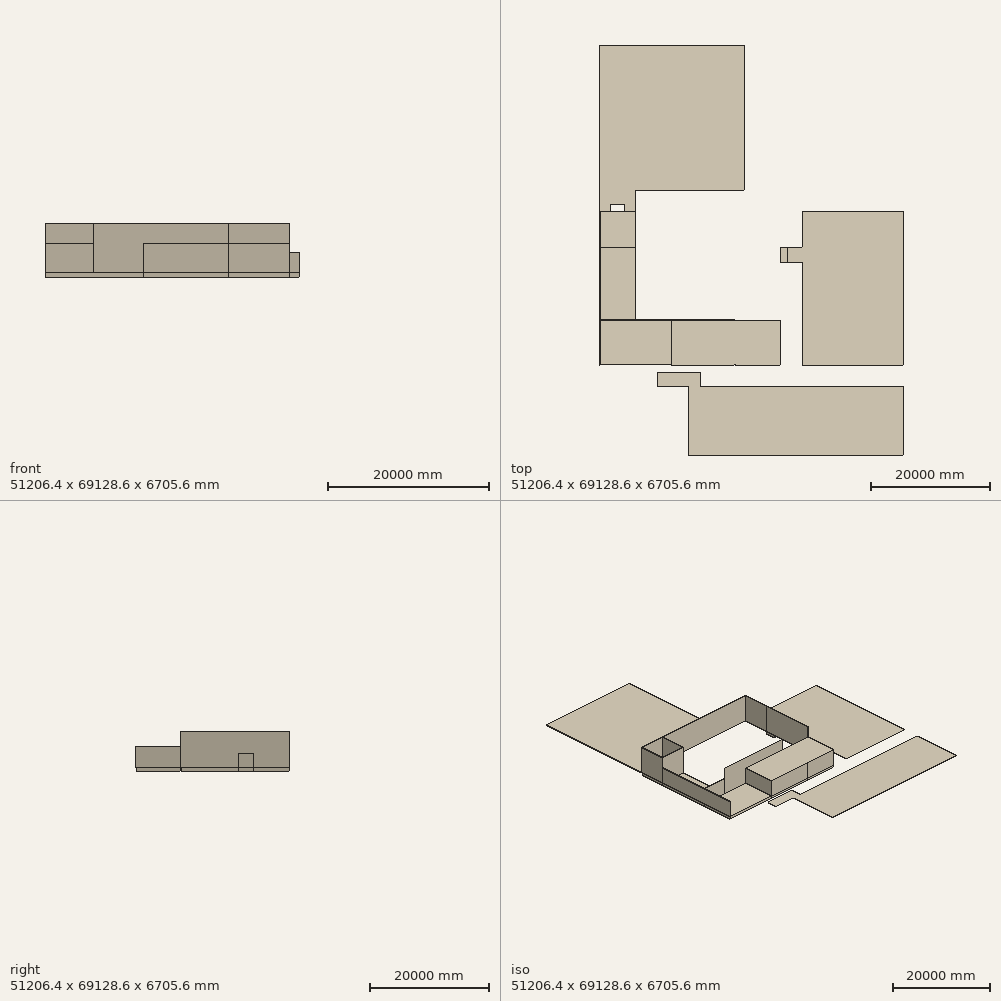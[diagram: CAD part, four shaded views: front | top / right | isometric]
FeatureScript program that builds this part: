
annotation { "Feature Type Name" : "Feature", "Feature Type Description" : "" }
export const myFeature = defineFeature(function(context is Context, id is Id, definition is map)
    precondition{}
    {
        {
            var Q0;
            Q0=qCreatedBy(makeId("Top.planeOp"),FACE);
            var sketch = newSketch(context, id + "F0", { "sketchPlane" : qUnion([Q0])});
            skLineSegment(sketch, "E0.bottom", {"start": v(-25389.28, -17373.6) * mm, "end": v(-36057.28, -17373.6) * mm});
            skLineSegment(sketch, "E0.left", {"start": v(-25389.28, -17373.6) * mm, "end": v(-25389.28, -9753.6) * mm});
            skLineSegment(sketch, "E0.right", {"start": v(-36057.28, -17373.6) * mm, "end": v(-36057.28, -9753.6) * mm});
            skLineSegment(sketch, "E1.bottom", {"start": v(-36057.28, -17373.6) * mm, "end": v(-48249.28, -17373.6) * mm});
            skLineSegment(sketch, "E1.top", {"start": v(-37581.28, -9753.6) * mm, "end": v(-48249.28, -9753.6) * mm});
            skLineSegment(sketch, "E1.right", {"start": v(-48249.28, -17373.6) * mm, "end": v(-48249.28, -9753.6) * mm});
            skLineSegment(sketch, "E2.top", {"start": v(-25389.28, -17373.6) * mm, "end": v(-17769.28, -17373.6) * mm});
            skLineSegment(sketch, "E2.left", {"start": v(-25389.28, -9753.6) * mm, "end": v(-25389.28, -17373.6) * mm});
            skLineSegment(sketch, "E3.bottom", {"start": v(-48249.28, -9753.6) * mm, "end": v(-42153.28, -9753.6) * mm});
            skLineSegment(sketch, "E3.top", {"start": v(-48249.28, 2438.4) * mm, "end": v(-42153.28, 2438.4) * mm});
            skLineSegment(sketch, "E3.left", {"start": v(-48249.28, -9753.6) * mm, "end": v(-48249.28, 2438.4) * mm});
            skLineSegment(sketch, "E3.right", {"start": v(-42153.28, -9753.6) * mm, "end": v(-42153.28, 2438.4) * mm});
            skLineSegment(sketch, "E4.bottom", {"start": v(-42153.28, -9753.6) * mm, "end": v(-17769.28, -9753.6) * mm});
            skLineSegment(sketch, "E4.top", {"start": v(-17830.23, 2438.4) * mm, "end": v(-17769.28, 2438.4) * mm});
            skLineSegment(sketch, "E4.right", {"start": v(-17769.28, -9753.6) * mm, "end": v(-17769.28, 2438.4) * mm});
            skLineSegment(sketch, "E5.top", {"start": v(-48249.28, 8534.4) * mm, "end": v(-42153.28, 8534.4) * mm});
            skLineSegment(sketch, "E5.left", {"start": v(-48249.28, 2438.4) * mm, "end": v(-48249.28, 8534.4) * mm});
            skLineSegment(sketch, "E5.right", {"start": v(-42153.28, 2438.4) * mm, "end": v(-42153.28, 8534.4) * mm});
            skLineSegment(sketch, "E6.bottom", {"start": v(-42153.28, 8534.4) * mm, "end": v(-36057.28, 8534.4) * mm});
            skLineSegment(sketch, "E6.left", {"start": v(-42153.28, 8534.4) * mm, "end": v(-42153.28, 2438.4) * mm});
            skLineSegment(sketch, "E6.right", {"start": v(-36057.28, 8534.4) * mm, "end": v(-36057.28, 8473.44) * mm});
            skLineSegment(sketch, "E7.bottom", {"start": v(-36057.28, 8534.4) * mm, "end": v(-31485.28, 8534.4) * mm});
            skLineSegment(sketch, "E7.right", {"start": v(-31485.28, 8534.4) * mm, "end": v(-31485.28, 8473.44) * mm});
            skLineSegment(sketch, "E8.bottom", {"start": v(-31485.28, 8534.4) * mm, "end": v(-17769.28, 8534.4) * mm});
            skLineSegment(sketch, "E8.right", {"start": v(-17769.28, 8534.4) * mm, "end": v(-17769.28, 2438.4) * mm});
            skLineSegment(sketch, "E9.bottom", {"start": v(-46420.48, 8534.4) * mm, "end": v(-43982.08, 8534.4) * mm});
            skLineSegment(sketch, "E9.top", {"start": v(-46420.48, 9753.6) * mm, "end": v(-43982.08, 9753.6) * mm});
            skLineSegment(sketch, "E9.left", {"start": v(-46420.48, 9753.6) * mm, "end": v(-46420.48, 8534.4) * mm});
            skLineSegment(sketch, "E9.right", {"start": v(-43982.08, 9753.6) * mm, "end": v(-43982.08, 8534.4) * mm});
            skLineSegment(sketch, "E10.bottom", {"start": v(-38495.68, -17373.6) * mm, "end": v(-36057.28, -17373.6) * mm});
            skLineSegment(sketch, "E10.top", {"start": v(-38495.68, -18592.8) * mm, "end": v(-36057.28, -18592.8) * mm});
            skLineSegment(sketch, "E10.left", {"start": v(-38495.68, -17373.6) * mm, "end": v(-38495.68, -18592.8) * mm});
            skLineSegment(sketch, "E10.right", {"start": v(-36057.28, -17373.6) * mm, "end": v(-36057.28, -18592.8) * mm});
            skLineSegment(sketch, "E11.bottom", {"start": v(-17769.28, 2438.4) * mm, "end": v(-16550.08, 2438.4) * mm});
            skLineSegment(sketch, "E11.top", {"start": v(-17769.28, 0) * mm, "end": v(-16550.08, 0) * mm});
            skLineSegment(sketch, "E11.left", {"start": v(-17769.28, 2438.4) * mm, "end": v(-17769.28, 0) * mm});
            skLineSegment(sketch, "E11.right", {"start": v(-16550.08, 2438.4) * mm, "end": v(-16550.08, 0) * mm});
            skLineSegment(sketch, "E12.0", {"start": v(-48188.32, 8473.44) * mm, "end": v(-42214.24, 8473.44) * mm});
            skLineSegment(sketch, "E12.1", {"start": v(-48188.32, 2499.36) * mm, "end": v(-48188.32, 8473.44) * mm});
            skLineSegment(sketch, "E12.2", {"start": v(-48188.32, 2499.36) * mm, "end": v(-42214.24, 2499.36) * mm});
            skLineSegment(sketch, "E12.3", {"start": v(-42214.24, 2499.36) * mm, "end": v(-42214.24, 8473.44) * mm});
            skLineSegment(sketch, "E13.1", {"start": v(-31485.28, 8473.44) * mm, "end": v(-17830.24, 8473.44) * mm});
            skLineSegment(sketch, "E13.2", {"start": v(-36057.28, 8473.44) * mm, "end": v(-31485.28, 8473.44) * mm});
            skLineSegment(sketch, "E13.3", {"start": v(-42153.28, 8473.44) * mm, "end": v(-36057.28, 8473.44) * mm});
            skLineSegment(sketch, "E14.0", {"start": v(-17830.23, -9753.6) * mm, "end": v(-17830.23, 2438.4) * mm});
            skLineSegment(sketch, "E15", {"start": v(-17769.28, -17373.6) * mm, "end": v(-17769.28, -9753.6) * mm});
            skLineSegment(sketch, "E16.0", {"start": v(-25389.28, -17312.64) * mm, "end": v(-36057.28, -17312.64) * mm});
            skLineSegment(sketch, "E16.1", {"start": v(-25389.28, -17312.64) * mm, "end": v(-17830.24, -17312.64) * mm});
            skLineSegment(sketch, "E16.2", {"start": v(-17830.24, -17312.64) * mm, "end": v(-17830.24, -9753.6) * mm});
            skLineSegment(sketch, "E17.0", {"start": v(-42153.28, -9814.56) * mm, "end": v(-17769.28, -9814.56) * mm});
            skLineSegment(sketch, "E18.0", {"start": v(-25450.24, -9753.6) * mm, "end": v(-25450.24, -17373.6) * mm});
            skLineSegment(sketch, "E19.0", {"start": v(-35996.32, -17373.6) * mm, "end": v(-35996.32, -9753.6) * mm});
            skLineSegment(sketch, "E20.0", {"start": v(-36057.28, -17312.64) * mm, "end": v(-48249.28, -17312.64) * mm});
            skLineSegment(sketch, "E21.0", {"start": v(-48188.32, -17373.6) * mm, "end": v(-48188.32, -9753.6) * mm});
            skLineSegment(sketch, "E22.0", {"start": v(-48188.32, -9753.6) * mm, "end": v(-48188.32, 2438.4) * mm});
            skLineSegment(sketch, "E23.0", {"start": v(-48249.28, -9814.56) * mm, "end": v(-42153.28, -9814.56) * mm});
            skLineSegment(sketch, "E24.0", {"start": v(-42214.24, -9753.6) * mm, "end": v(-42214.24, 2438.4) * mm});
            skLineSegment(sketch, "E25", {"start": v(-17830.24, 8473.44) * mm, "end": v(-17769.28, 8534.4) * mm});
            skLineSegment(sketch, "E26", {"start": v(-17830.23, 2438.4) * mm, "end": v(-17830.24, 8473.44) * mm});
            skLineSegment(sketch, "E27", {"start": v(-42214.24, -9753.6) * mm, "end": v(-42214.24, -9814.56) * mm});
            skLineSegment(sketch, "E28.bottom", {"start": v(-14111.68, 8473.44) * mm, "end": v(2957.12, 8473.44) * mm});
            skLineSegment(sketch, "E28.top", {"start": v(-14111.68, -17434.56) * mm, "end": v(2957.12, -17434.56) * mm});
            skLineSegment(sketch, "E28.left", {"start": v(-14111.68, 8473.44) * mm, "end": v(-14111.68, -17434.56) * mm});
            skLineSegment(sketch, "E28.right", {"start": v(2957.12, 8473.44) * mm, "end": v(2957.12, -17434.56) * mm});
            skLineSegment(sketch, "E29.bottom", {"start": v(-33314.08, -32613.6) * mm, "end": v(2957.12, -32613.6) * mm});
            skLineSegment(sketch, "E29.top", {"start": v(-33314.08, -21031.2) * mm, "end": v(2957.12, -21031.2) * mm});
            skLineSegment(sketch, "E29.left", {"start": v(-33314.08, -32613.6) * mm, "end": v(-33314.08, -21031.2) * mm});
            skLineSegment(sketch, "E29.right", {"start": v(2957.12, -32613.6) * mm, "end": v(2957.12, -21031.2) * mm});
            skLineSegment(sketch, "E30.top", {"start": v(-14111.68, -21031.2) * mm, "end": v(2957.12, -21031.2) * mm});
            skLineSegment(sketch, "E30.left", {"start": v(-14111.68, -17434.56) * mm, "end": v(-14111.68, -21031.2) * mm});
            skLineSegment(sketch, "E30.right", {"start": v(2957.12, -17434.56) * mm, "end": v(2957.12, -21031.2) * mm});
            skLineSegment(sketch, "E31.bottom", {"start": v(-8625.28, 8473.44) * mm, "end": v(-2529.28, 8473.44) * mm});
            skLineSegment(sketch, "E31.top", {"start": v(-8625.28, 42001.44) * mm, "end": v(-2529.28, 42001.44) * mm});
            skLineSegment(sketch, "E31.left", {"start": v(-8625.28, 8473.44) * mm, "end": v(-8625.28, 42001.44) * mm});
            skLineSegment(sketch, "E31.right", {"start": v(-2529.28, 8473.44) * mm, "end": v(-2529.28, 42001.44) * mm});
            skLineSegment(sketch, "E32.bottom", {"start": v(-48249.28, 36515.04) * mm, "end": v(-23865.28, 36515.04) * mm});
            skLineSegment(sketch, "E32.top", {"start": v(-48249.28, 12131.04) * mm, "end": v(-23865.28, 12131.04) * mm});
            skLineSegment(sketch, "E32.left", {"start": v(-48249.28, 36515.04) * mm, "end": v(-48249.28, 12131.04) * mm});
            skLineSegment(sketch, "E32.right", {"start": v(-23865.28, 36515.04) * mm, "end": v(-23865.28, 12131.04) * mm});
            skLineSegment(sketch, "E33.bottom", {"start": v(-23865.28, 36515.04) * mm, "end": v(-34533.28, 36515.04) * mm});
            skLineSegment(sketch, "E33.top", {"start": v(-23865.28, 42611.04) * mm, "end": v(-34533.28, 42611.04) * mm});
            skLineSegment(sketch, "E33.left", {"start": v(-23865.28, 36515.04) * mm, "end": v(-23865.28, 42611.04) * mm});
            skLineSegment(sketch, "E33.right", {"start": v(-34533.28, 36515.04) * mm, "end": v(-34533.28, 42611.04) * mm});
            skLineSegment(sketch, "E34.bottom", {"start": v(-48249.28, 12131.04) * mm, "end": v(-42153.28, 12131.04) * mm});
            skLineSegment(sketch, "E34.left", {"start": v(-48249.28, 12131.04) * mm, "end": v(-48249.28, 8534.4) * mm});
            skLineSegment(sketch, "E34.right", {"start": v(-42153.28, 12131.04) * mm, "end": v(-42153.28, 8534.4) * mm});
            skLineSegment(sketch, "E35.bottom", {"start": v(-16550.08, 2438.4) * mm, "end": v(-14111.68, 2438.4) * mm});
            skLineSegment(sketch, "E35.top", {"start": v(-16550.08, 0) * mm, "end": v(-14111.68, 0) * mm});
            skLineSegment(sketch, "E35.right", {"start": v(-14111.68, 2438.4) * mm, "end": v(-14111.68, 0) * mm});
            skLineSegment(sketch, "E36.bottom", {"start": v(-38495.68, -18592.8) * mm, "end": v(-31248.17, -18592.8) * mm});
            skLineSegment(sketch, "E36.top", {"start": v(-38495.68, -21031.2) * mm, "end": v(-31248.17, -21031.2) * mm});
            skLineSegment(sketch, "E36.left", {"start": v(-38495.68, -18592.8) * mm, "end": v(-38495.68, -21031.2) * mm});
            skLineSegment(sketch, "E36.right", {"start": v(-31248.17, -18592.8) * mm, "end": v(-31248.17, -21031.2) * mm});
            skSolve(sketch);
        }
        {
            var Q0;
            {var subQ1=sQuery(id+"F0.wireOp",EDGE,"E2.left");var subQ3=sQuery(id+"F0.wireOp",EDGE,"E17.0");var subQ4=makeQuery(id+"F0.imprint","INTERSECT",VERTEX,{"derivedFrom":[subQ1,subQ3]});Q0=makeQuery(id+"F0.imprint","IMPRINT",FACE,{"disambiguationData":[TD([[makeQuery(id+"F0.imprint","IMPRINT",EDGE,{"disambiguationData":[TD([[subQ4,1.0]])],"derivedFrom":subQ3}),-1.0]])]});}
            var Q1;
            {var subQ0=sQuery(id+"F0.wireOp",EDGE,"E4.bottom");var subQ1=sQuery(id+"F0.wireOp",EDGE,"E2.left");var subQ2=makeQuery(id+"F0.imprint","INTERSECT",VERTEX,{"derivedFrom":[subQ1,subQ0]});Q1=makeQuery(id+"F0.imprint","IMPRINT",FACE,{"disambiguationData":[TD([[makeQuery(id+"F0.imprint","IMPRINT",EDGE,{"disambiguationData":[TD([[subQ2,-1.0]])],"derivedFrom":subQ1}),-1.0]])]});}
            var Q2;
            {var subQ0=sQuery(id+"F0.wireOp",EDGE,"E18.0");var subQ1=sQuery(id+"F0.wireOp",EDGE,"E4.bottom");var subQ2=makeQuery(id+"F0.imprint","INTERSECT",VERTEX,{"derivedFrom":[subQ1,subQ0]});Q2=makeQuery(id+"F0.imprint","IMPRINT",FACE,{"disambiguationData":[TD([[makeQuery(id+"F0.imprint","IMPRINT",EDGE,{"disambiguationData":[TD([[subQ2,1.0]])],"derivedFrom":subQ1}),-1.0]])]});}
            var Q3;
            {var subQ0=sQuery(id+"F0.wireOp",EDGE,"E4.bottom");var subQ13=makeQuery(id+"F0.imprint","IMPRINT",VERTEX,{"derivedFrom":subQ0});Q3=makeQuery(id+"F0.imprint","IMPRINT",FACE,{"disambiguationData":[TD([[makeQuery(id+"F0.imprint","IMPRINT",EDGE,{"disambiguationData":[TD([[subQ13,-1.0]])],"derivedFrom":subQ0}),-1.0]])]});}
            var Q4;
            {var subQ0=sQuery(id+"F0.wireOp",EDGE,"E3.bottom");var subQ5=sQuery(id+"F0.wireOp",EDGE,"E21.0");var subQ6=makeQuery(id+"F0.imprint","INTERSECT",VERTEX,{"derivedFrom":[subQ0,subQ5]});Q4=makeQuery(id+"F0.imprint","IMPRINT",FACE,{"disambiguationData":[TD([[makeQuery(id+"F0.imprint","IMPRINT",EDGE,{"disambiguationData":[TD([[subQ6,1.0]])],"derivedFrom":subQ5}),1.0]])]});}
            var Q5;
            {var subQ0=sQuery(id+"F0.wireOp",EDGE,"E3.left");Q5=makeQuery(id+"F0.imprint","IMPRINT",FACE,{"disambiguationData":[TD([[makeQuery(id+"F0.imprint","IMPRINT",EDGE,{"derivedFrom":subQ0}),-1.0]])]});}
            var Q6;
            {var subQ0=sQuery(id+"F0.wireOp",EDGE,"E20.0");var subQ1=sQuery(id+"F0.wireOp",EDGE,"E1.right");var subQ2=makeQuery(id+"F0.imprint","INTERSECT",VERTEX,{"derivedFrom":[subQ1,subQ0]});Q6=makeQuery(id+"F0.imprint","IMPRINT",FACE,{"disambiguationData":[TD([[makeQuery(id+"F0.imprint","IMPRINT",EDGE,{"disambiguationData":[TD([[subQ2,-1.0]])],"derivedFrom":subQ1}),-1.0]])]});}
            var Q7;
            {var subQ0=sQuery(id+"F0.wireOp",EDGE,"E10.bottom");Q7=makeQuery(id+"F0.imprint","IMPRINT",FACE,{"disambiguationData":[TD([[makeQuery(id+"F0.imprint","IMPRINT",EDGE,{"derivedFrom":subQ0}),1.0]])]});}
            var Q8;
            {var subQ0=sQuery(id+"F0.wireOp",EDGE,"E0.right");var subQ5=sQuery(id+"F0.wireOp",EDGE,"E16.0");var subQ7=makeQuery(id+"F0.imprint","INTERSECT",VERTEX,{"derivedFrom":[subQ0,subQ5]});Q8=makeQuery(id+"F0.imprint","IMPRINT",FACE,{"disambiguationData":[TD([[makeQuery(id+"F0.imprint","IMPRINT",EDGE,{"disambiguationData":[TD([[subQ7,1.0]])],"derivedFrom":subQ5}),1.0]])]});}
            var Q9;
            {var subQ0=sQuery(id+"F0.wireOp",EDGE,"E0.right");var subQ6=sQuery(id+"F0.wireOp",EDGE,"E16.0");var subQ7=makeQuery(id+"F0.imprint","INTERSECT",VERTEX,{"derivedFrom":[subQ0,subQ6]});Q9=makeQuery(id+"F0.imprint","IMPRINT",FACE,{"disambiguationData":[TD([[makeQuery(id+"F0.imprint","IMPRINT",EDGE,{"disambiguationData":[TD([[subQ7,-1.0]])],"derivedFrom":subQ0}),-1.0]])]});}
            var Q10;
            {var subQ0=sQuery(id+"F0.wireOp",EDGE,"E18.0");var subQ1=sQuery(id+"F0.wireOp",EDGE,"E0.bottom");var subQ2=makeQuery(id+"F0.imprint","INTERSECT",VERTEX,{"derivedFrom":[subQ1,subQ0]});Q10=makeQuery(id+"F0.imprint","IMPRINT",FACE,{"disambiguationData":[TD([[makeQuery(id+"F0.imprint","IMPRINT",EDGE,{"disambiguationData":[TD([[subQ2,-1.0]])],"derivedFrom":subQ1}),-1.0]])]});}
            var Q11;
            {var subQ2=sQuery(id+"F0.wireOp",EDGE,"E2.top");Q11=makeQuery(id+"F0.imprint","IMPRINT",FACE,{"disambiguationData":[TD([[makeQuery(id+"F0.imprint","IMPRINT",EDGE,{"derivedFrom":subQ2}),1.0]])]});}
            var Q12;
            {var subQ0=sQuery(id+"F0.wireOp",EDGE,"E4.bottom");var subQ1=sQuery(id+"F0.wireOp",EDGE,"E2.left");var subQ2=makeQuery(id+"F0.imprint","INTERSECT",VERTEX,{"derivedFrom":[subQ1,subQ0]});Q12=makeQuery(id+"F0.imprint","IMPRINT",FACE,{"disambiguationData":[TD([[makeQuery(id+"F0.imprint","IMPRINT",EDGE,{"disambiguationData":[TD([[subQ2,-1.0]])],"derivedFrom":subQ1}),1.0]])]});}
            var Q13;
            {var subQ5=sQuery(id+"F0.wireOp",EDGE,"E27");Q13=makeQuery(id+"F0.imprint","IMPRINT",FACE,{"disambiguationData":[TD([[makeQuery(id+"F0.imprint","IMPRINT",EDGE,{"derivedFrom":subQ5}),-1.0]])]});}
            extrude(context, id + "F1", {"entities" : qUnion([Q0, Q1, Q2, Q3, Q4, Q5, Q6, Q7, Q8, Q9, Q10, Q11, Q12, Q13]), "depth" : 3657.6 * mm, "offsetDistance" : 30.48 * mm});
        }
        {
            var Q0;
            {var subQ0=sQuery(id+"F0.wireOp",EDGE,"E4.right");Q0=makeQuery(id+"F0.imprint","IMPRINT",FACE,{"disambiguationData":[TD([[makeQuery(id+"F0.imprint","IMPRINT",EDGE,{"derivedFrom":subQ0}),1.0]])]});}
            var Q1;
            Q1=makeQuery(id+"F0.imprint","IMPRINT",FACE,{"disambiguationData":[TD([[makeQuery(id+"F0.imprint","IMPRINT",EDGE,{"derivedFrom":sQuery(id+"F0.wireOp",EDGE,"E8.bottom")}),-1.0]])]});
            var Q2;
            {var subQ7=sQuery(id+"F0.wireOp",EDGE,"E5.left");Q2=makeQuery(id+"F0.imprint","IMPRINT",FACE,{"disambiguationData":[TD([[makeQuery(id+"F0.imprint","IMPRINT",EDGE,{"derivedFrom":subQ7}),-1.0]])]});}
            var Q3;
            {var subQ0=sQuery(id+"F0.wireOp",EDGE,"E6.bottom");Q3=makeQuery(id+"F0.imprint","IMPRINT",FACE,{"disambiguationData":[TD([[makeQuery(id+"F0.imprint","IMPRINT",EDGE,{"derivedFrom":subQ0}),-1.0]])]});}
            var Q4;
            Q4=makeQuery(id+"F0.imprint","IMPRINT",FACE,{"disambiguationData":[TD([[makeQuery(id+"F0.imprint","IMPRINT",EDGE,{"derivedFrom":sQuery(id+"F0.wireOp",EDGE,"E7.bottom")}),-1.0]])]});
            var Q5;
            Q5=makeQuery(id+"F0.imprint","IMPRINT",FACE,{"disambiguationData":[TD([[makeQuery(id+"F0.imprint","IMPRINT",EDGE,{"derivedFrom":sQuery(id+"F0.wireOp",EDGE,"E4.top")}),1.0]])]});
            var Q6;
            {var subQ1=sQuery(id+"F0.wireOp",EDGE,"E4.bottom");var subQ7=makeQuery(id+"F0.imprint","INTERSECT",VERTEX,{"derivedFrom":[subQ1,sQuery(id+"F0.wireOp",EDGE,"E14.0")]});Q6=makeQuery(id+"F0.imprint","IMPRINT",FACE,{"disambiguationData":[TD([[makeQuery(id+"F0.imprint","IMPRINT",EDGE,{"disambiguationData":[TD([[subQ7,1.0]])],"derivedFrom":subQ1}),-1.0]])]});}
            var Q7;
            {var subQ0=sQuery(id+"F0.wireOp",EDGE,"E4.bottom");var subQ1=sQuery(id+"F0.wireOp",EDGE,"E2.left");var subQ2=makeQuery(id+"F0.imprint","INTERSECT",VERTEX,{"derivedFrom":[subQ1,subQ0]});Q7=makeQuery(id+"F0.imprint","IMPRINT",FACE,{"disambiguationData":[TD([[makeQuery(id+"F0.imprint","IMPRINT",EDGE,{"disambiguationData":[TD([[subQ2,-1.0]])],"derivedFrom":subQ1}),1.0]])]});}
            var Q8;
            {var subQ0=sQuery(id+"F0.wireOp",EDGE,"E4.bottom");var subQ1=sQuery(id+"F0.wireOp",EDGE,"E2.left");var subQ2=makeQuery(id+"F0.imprint","INTERSECT",VERTEX,{"derivedFrom":[subQ1,subQ0]});Q8=makeQuery(id+"F0.imprint","IMPRINT",FACE,{"disambiguationData":[TD([[makeQuery(id+"F0.imprint","IMPRINT",EDGE,{"disambiguationData":[TD([[subQ2,-1.0]])],"derivedFrom":subQ1}),-1.0]])]});}
            var Q9;
            {var subQ0=sQuery(id+"F0.wireOp",EDGE,"E18.0");var subQ1=sQuery(id+"F0.wireOp",EDGE,"E4.bottom");var subQ2=makeQuery(id+"F0.imprint","INTERSECT",VERTEX,{"derivedFrom":[subQ1,subQ0]});Q9=makeQuery(id+"F0.imprint","IMPRINT",FACE,{"disambiguationData":[TD([[makeQuery(id+"F0.imprint","IMPRINT",EDGE,{"disambiguationData":[TD([[subQ2,1.0]])],"derivedFrom":subQ1}),-1.0]])]});}
            var Q10;
            {var subQ0=sQuery(id+"F0.wireOp",EDGE,"E4.bottom");var subQ1=sQuery(id+"F0.wireOp",EDGE,"E0.right");var subQ2=makeQuery(id+"F0.imprint","INTERSECT",VERTEX,{"derivedFrom":[subQ1,subQ0]});Q10=makeQuery(id+"F0.imprint","IMPRINT",FACE,{"disambiguationData":[TD([[makeQuery(id+"F0.imprint","IMPRINT",EDGE,{"disambiguationData":[TD([[subQ2,1.0]])],"derivedFrom":subQ1}),-1.0]])]});}
            var Q11;
            {var subQ0=sQuery(id+"F0.wireOp",EDGE,"E3.right");Q11=makeQuery(id+"F0.imprint","IMPRINT",FACE,{"disambiguationData":[TD([[makeQuery(id+"F0.imprint","IMPRINT",EDGE,{"derivedFrom":subQ0}),1.0]])]});}
            var Q12;
            {var subQ6=sQuery(id+"F0.wireOp",EDGE,"E27");Q12=makeQuery(id+"F0.imprint","IMPRINT",FACE,{"disambiguationData":[TD([[makeQuery(id+"F0.imprint","IMPRINT",EDGE,{"derivedFrom":subQ6}),1.0]])]});}
            extrude(context, id + "F2", {"entities" : qUnion([Q0, Q1, Q2, Q3, Q4, Q5, Q6, Q7, Q8, Q9, Q10, Q11, Q12]), "depth" : 6096 * mm, "offsetDistance" : 30.48 * mm});
        }
        {
            var Q0;
            Q0=makeQuery(id+"F0.imprint","IMPRINT",FACE,{"disambiguationData":[TD([[makeQuery(id+"F0.imprint","IMPRINT",EDGE,{"derivedFrom":sQuery(id+"F0.wireOp",EDGE,"E10.bottom")}),-1.0]])]});
            var Q1;
            Q1=makeQuery(id+"F0.imprint","IMPRINT",FACE,{"disambiguationData":[TD([[makeQuery(id+"F0.imprint","IMPRINT",EDGE,{"derivedFrom":sQuery(id+"F0.wireOp",EDGE,"E11.bottom")}),-1.0]])]});
            var Q2;
            Q2=makeQuery(id+"F0.imprint","IMPRINT",FACE,{"disambiguationData":[TD([[makeQuery(id+"F0.imprint","IMPRINT",EDGE,{"derivedFrom":sQuery(id+"F0.wireOp",EDGE,"E9.bottom")}),1.0]])]});
            extrude(context, id + "F3", {"entities" : qUnion([Q0, Q1, Q2]), "depth" : 2438.4 * mm, "offsetDistance" : 30.48 * mm});
        }
        {
            var Q0;
            {var subQ1=sQuery(id+"F0.wireOp",EDGE,"E3.right");Q0=makeQuery(id+"F0.imprint","IMPRINT",FACE,{"disambiguationData":[TD([[makeQuery(id+"F0.imprint","IMPRINT",EDGE,{"derivedFrom":subQ1}),-1.0]])]});}
            var Q1;
            {var subQ0=sQuery(id+"F0.wireOp",EDGE,"E16.1");Q1=makeQuery(id+"F0.imprint","IMPRINT",FACE,{"disambiguationData":[TD([[makeQuery(id+"F0.imprint","IMPRINT",EDGE,{"derivedFrom":subQ0}),1.0]])]});}
            var Q2;
            {var subQ0=sQuery(id+"F0.wireOp",EDGE,"E18.0");var subQ1=sQuery(id+"F0.wireOp",EDGE,"E16.0");var subQ2=makeQuery(id+"F0.imprint","INTERSECT",VERTEX,{"derivedFrom":[subQ1,subQ0]});Q2=makeQuery(id+"F0.imprint","IMPRINT",FACE,{"disambiguationData":[TD([[makeQuery(id+"F0.imprint","IMPRINT",EDGE,{"disambiguationData":[TD([[subQ2,-1.0]])],"derivedFrom":subQ1}),-1.0]])]});}
            var Q3;
            {var subQ0=sQuery(id+"F0.wireOp",EDGE,"E20.0");var subQ1=sQuery(id+"F0.wireOp",EDGE,"E0.right");var subQ2=makeQuery(id+"F0.imprint","INTERSECT",VERTEX,{"derivedFrom":[subQ1,subQ0]});Q3=makeQuery(id+"F0.imprint","IMPRINT",FACE,{"disambiguationData":[TD([[makeQuery(id+"F0.imprint","IMPRINT",EDGE,{"disambiguationData":[TD([[subQ2,-1.0]])],"derivedFrom":subQ1}),1.0]])]});}
            var Q4;
            {var subQ0=sQuery(id+"F0.wireOp",EDGE,"E22.0");Q4=makeQuery(id+"F0.imprint","IMPRINT",FACE,{"disambiguationData":[TD([[makeQuery(id+"F0.imprint","IMPRINT",EDGE,{"derivedFrom":subQ0}),-1.0]])]});}
            var Q5;
            Q5=makeQuery(id+"F0.imprint","IMPRINT",FACE,{"disambiguationData":[TD([[makeQuery(id+"F0.imprint","IMPRINT",EDGE,{"derivedFrom":sQuery(id+"F0.wireOp",EDGE,"E12.0")}),-1.0]])]});
            var Q6;
            Q6=makeQuery(id+"F0.imprint","IMPRINT",FACE,{"disambiguationData":[TD([[makeQuery(id+"F0.imprint","IMPRINT",EDGE,{"derivedFrom":sQuery(id+"F0.wireOp",EDGE,"E9.bottom")}),1.0]])]});
            var Q7;
            Q7=makeQuery(id+"F0.imprint","IMPRINT",FACE,{"disambiguationData":[TD([[makeQuery(id+"F0.imprint","IMPRINT",EDGE,{"derivedFrom":sQuery(id+"F0.wireOp",EDGE,"E10.bottom")}),-1.0]])]});
            var Q8;
            Q8=makeQuery(id+"F0.imprint","IMPRINT",FACE,{"disambiguationData":[TD([[makeQuery(id+"F0.imprint","IMPRINT",EDGE,{"derivedFrom":sQuery(id+"F0.wireOp",EDGE,"E11.bottom")}),-1.0]])]});
            extrude(context, id + "F4", {"entities" : qUnion([Q0, Q1, Q2, Q3, Q4, Q5, Q6, Q7, Q8]), "oppositeDirection" : true, "depth" : 609.6 * mm, "offsetDistance" : 30.48 * mm});
        }
        {
            var Q0;
            Q0=makeQuery(id+"F0.imprint","IMPRINT",FACE,{"disambiguationData":[TD([[makeQuery(id+"F0.imprint","IMPRINT",EDGE,{"derivedFrom":sQuery(id+"F0.wireOp",EDGE,"E28.bottom")}),-1.0]])]});
            var Q1;
            Q1=makeQuery(id+"F0.imprint","IMPRINT",FACE,{"disambiguationData":[TD([[makeQuery(id+"F0.imprint","IMPRINT",EDGE,{"derivedFrom":sQuery(id+"F0.wireOp",EDGE,"E28.top")}),-1.0]])]});
            var Q2;
            Q2=makeQuery(id+"F0.imprint","IMPRINT",FACE,{"disambiguationData":[TD([[makeQuery(id+"F0.imprint","IMPRINT",EDGE,{"derivedFrom":sQuery(id+"F0.wireOp",EDGE,"E29.bottom")}),1.0]])]});
            var Q3;
            Q3=makeQuery(id+"F0.imprint","IMPRINT",FACE,{"disambiguationData":[TD([[makeQuery(id+"F0.imprint","IMPRINT",EDGE,{"derivedFrom":sQuery(id+"F0.wireOp",EDGE,"E31.bottom")}),1.0]])]});
            var Q4;
            Q4=makeQuery(id+"F0.imprint","IMPRINT",FACE,{"disambiguationData":[TD([[makeQuery(id+"F0.imprint","IMPRINT",EDGE,{"derivedFrom":sQuery(id+"F0.wireOp",EDGE,"E32.bottom")}),-1.0]])]});
            var Q5;
            Q5=makeQuery(id+"F0.imprint","IMPRINT",FACE,{"disambiguationData":[TD([[makeQuery(id+"F0.imprint","IMPRINT",EDGE,{"derivedFrom":sQuery(id+"F0.wireOp",EDGE,"E33.bottom")}),-1.0]])]});
            var Q6;
            Q6=makeQuery(id+"F0.imprint","IMPRINT",FACE,{"disambiguationData":[TD([[makeQuery(id+"F0.imprint","IMPRINT",EDGE,{"derivedFrom":sQuery(id+"F0.wireOp",EDGE,"E9.top")}),1.0]])]});
            var Q7;
            {var subQ3=sQuery(id+"F0.wireOp",EDGE,"E36.left");Q7=makeQuery(id+"F0.imprint","IMPRINT",FACE,{"disambiguationData":[TD([[makeQuery(id+"F0.imprint","IMPRINT",EDGE,{"derivedFrom":subQ3}),1.0]])]});}
            var Q8;
            Q8=makeQuery(id+"F0.imprint","IMPRINT",FACE,{"disambiguationData":[TD([[makeQuery(id+"F0.imprint","IMPRINT",EDGE,{"derivedFrom":sQuery(id+"F0.wireOp",EDGE,"E35.bottom")}),-1.0]])]});
            extrude(context, id + "F5", {"entities" : qUnion([Q0, Q1, Q2, Q3, Q4, Q5, Q6, Q7, Q8]), "oppositeDirection" : true, "depth" : 30.48 * mm, "offsetDistance" : 30.48 * mm});
        }
    });
